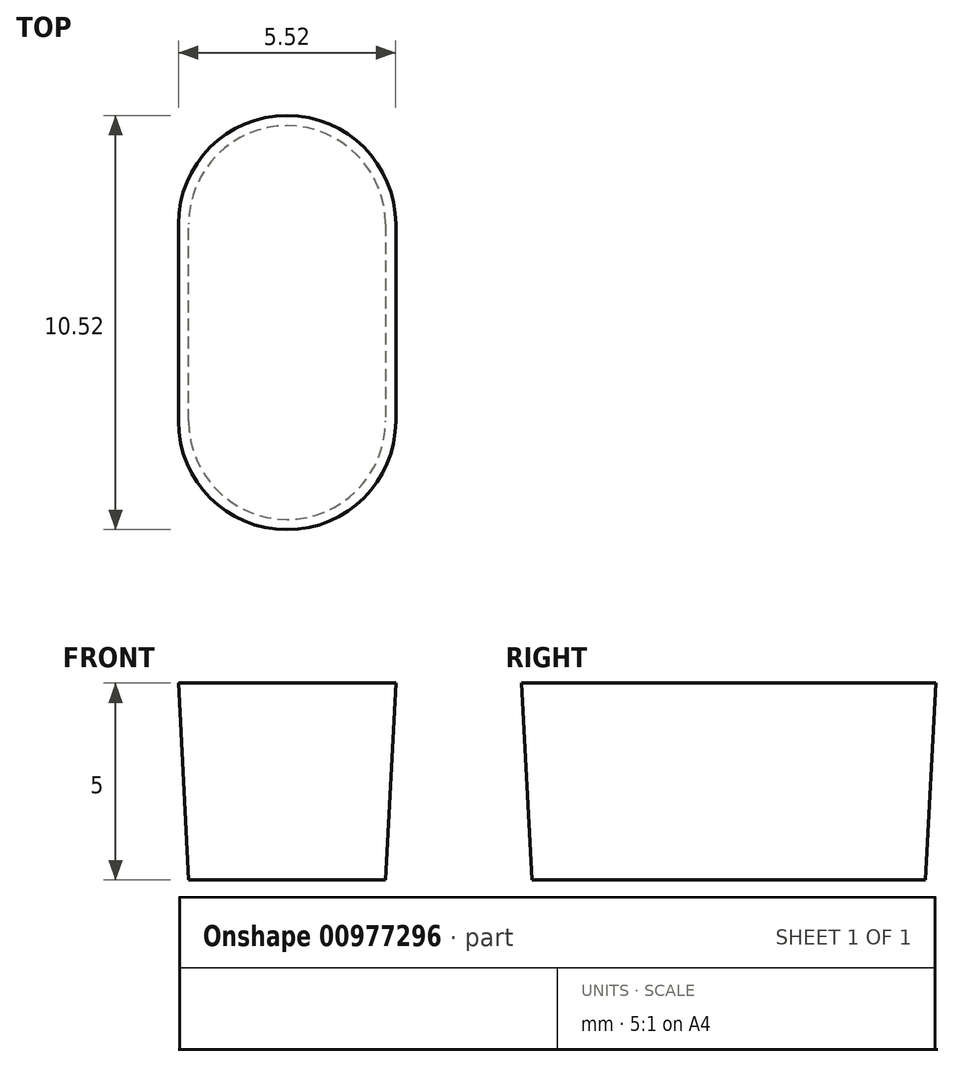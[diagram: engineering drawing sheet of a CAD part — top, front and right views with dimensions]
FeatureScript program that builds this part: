
annotation { "Feature Type Name" : "Feature", "Feature Type Description" : "" }
export const myFeature = defineFeature(function(context is Context, id is Id, definition is map)
    precondition{}
    {
        {
            var Q0;
            Q0=qCreatedBy(makeId("Top.planeOp"),FACE);
            var sketch = newSketch(context, id + "F0", { "sketchPlane" : qUnion([Q0])});
            skLineSegment(sketch, "E0.bottom", {"start": v(-2.5, 2.5) * mm, "end": v(2.5, 2.5) * mm});
            skLineSegment(sketch, "E0.top", {"start": v(-2.5, -2.5) * mm, "end": v(2.5, -2.5) * mm});
            skLineSegment(sketch, "E0.left", {"start": v(-2.5, 2.5) * mm, "end": v(-2.5, -2.5) * mm});
            skLineSegment(sketch, "E0.right", {"start": v(2.5, 2.5) * mm, "end": v(2.5, -2.5) * mm});
            skPoint(sketch, "E0.middle", {"position": v(0, 0) * mm});
            skCircle(sketch, "E1", {"center": v(0, 2.5) * mm, "radius": 2.5 * mm});
            skCircle(sketch, "E2", {"center": v(0, -2.5) * mm, "radius": 2.5 * mm});
            skSolve(sketch);
        }
        {
            var Q0;
            {var subQ0=sQuery(id+"F0.wireOp",EDGE,"E0.bottom");Q0=makeQuery(id+"F0.imprint","IMPRINT",FACE,{"disambiguationData":[TD([[makeQuery(id+"F0.imprint","IMPRINT",EDGE,{"derivedFrom":subQ0}),1.0]])]});}
            var Q1;
            {var subQ0=sQuery(id+"F0.wireOp",EDGE,"E0.bottom");Q1=makeQuery(id+"F0.imprint","IMPRINT",FACE,{"disambiguationData":[TD([[makeQuery(id+"F0.imprint","IMPRINT",EDGE,{"derivedFrom":subQ0}),-1.0]])]});}
            var Q2;
            {var subQ0=sQuery(id+"F0.wireOp",EDGE,"E0.right");Q2=makeQuery(id+"F0.imprint","IMPRINT",FACE,{"disambiguationData":[TD([[makeQuery(id+"F0.imprint","IMPRINT",EDGE,{"derivedFrom":subQ0}),-1.0]])]});}
            var Q3;
            {var subQ0=sQuery(id+"F0.wireOp",EDGE,"E0.left");Q3=makeQuery(id+"F0.imprint","IMPRINT",FACE,{"disambiguationData":[TD([[makeQuery(id+"F0.imprint","IMPRINT",EDGE,{"derivedFrom":subQ0}),1.0]])]});}
            var Q4;
            {var subQ0=sQuery(id+"F0.wireOp",EDGE,"E0.top");Q4=makeQuery(id+"F0.imprint","IMPRINT",FACE,{"disambiguationData":[TD([[makeQuery(id+"F0.imprint","IMPRINT",EDGE,{"derivedFrom":subQ0}),1.0]])]});}
            var Q5;
            {var subQ0=sQuery(id+"F0.wireOp",EDGE,"E0.top");Q5=makeQuery(id+"F0.imprint","IMPRINT",FACE,{"disambiguationData":[TD([[makeQuery(id+"F0.imprint","IMPRINT",EDGE,{"derivedFrom":subQ0}),-1.0]])]});}
            extrude(context, id + "F1", {"entities" : qUnion([Q0, Q1, Q2, Q3, Q4, Q5]), "depth" : 5 * mm, "offsetDistance" : 25 * mm, "hasDraft" : true, "draftAngle" : 3 * degree});
        }
    });
